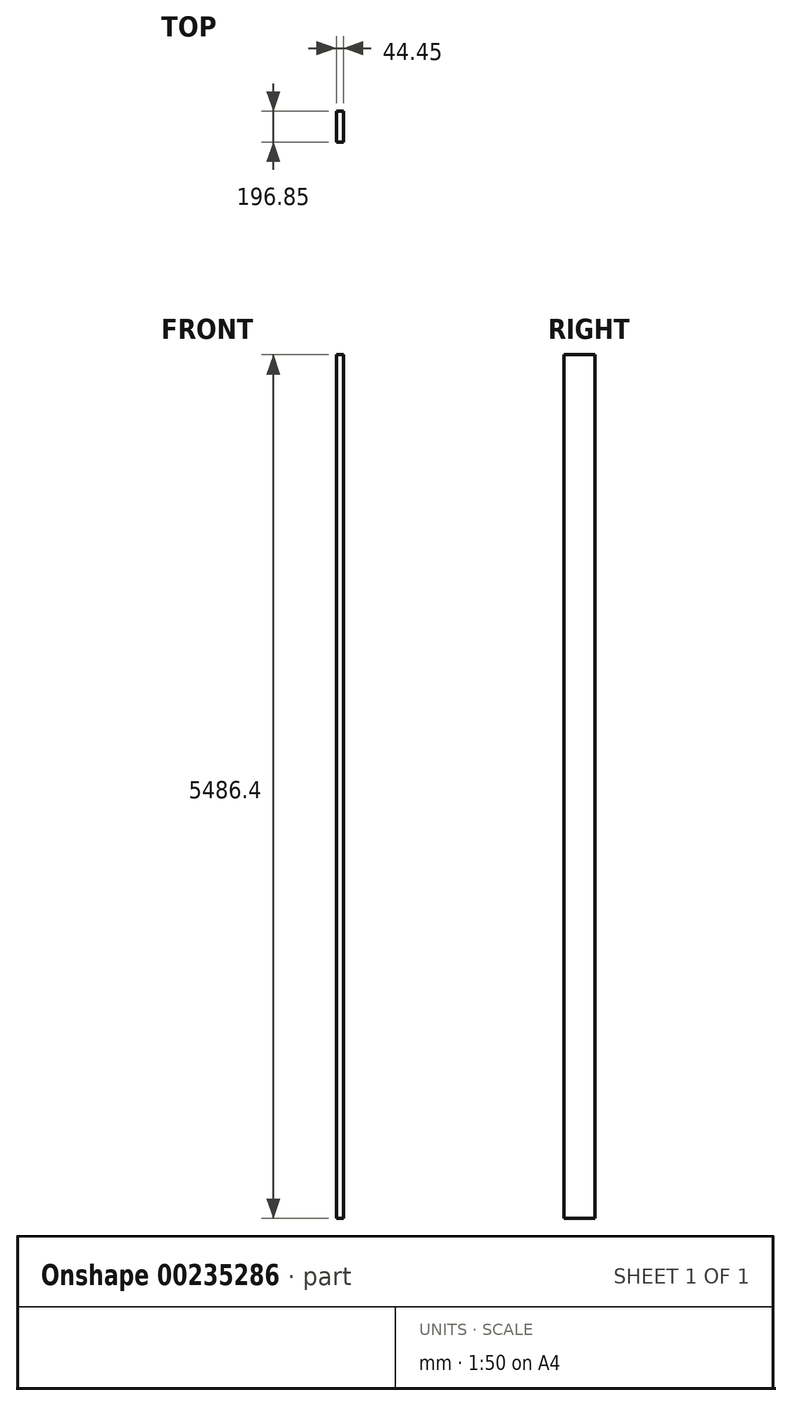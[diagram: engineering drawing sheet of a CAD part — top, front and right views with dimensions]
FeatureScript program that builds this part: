
annotation { "Feature Type Name" : "Feature", "Feature Type Description" : "" }
export const myFeature = defineFeature(function(context is Context, id is Id, definition is map)
    precondition{}
    {
        {
            var Q0;
            Q0=qCreatedBy(makeId("Top.planeOp"),FACE);
            var sketch = newSketch(context, id + "F0", { "sketchPlane" : qUnion([Q0])});
            skLineSegment(sketch, "E0", {"start": v(0, 0) * mm, "end": v(44.45, 0) * mm});
            skLineSegment(sketch, "E1", {"start": v(44.45, 0) * mm, "end": v(44.45, 196.85) * mm});
            skLineSegment(sketch, "E2", {"start": v(44.45, 196.85) * mm, "end": v(0, 196.85) * mm});
            skLineSegment(sketch, "E3", {"start": v(0, 196.85) * mm, "end": v(0, 0) * mm});
            skSolve(sketch);
        }
        {
            var Q0;
            Q0=makeQuery(id+"F0.imprint","IMPRINT",FACE,{"disambiguationData":[TD([[makeQuery(id+"F0.imprint","IMPRINT",EDGE,{"derivedFrom":sQuery(id+"F0.wireOp",EDGE,"E0")}),1.0]])]});
            extrude(context, id + "F1", {"entities" : qUnion([Q0]), "depth" : 5486.4 * mm, "offsetDistance" : 25.4 * mm});
        }
    });
